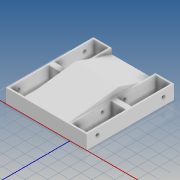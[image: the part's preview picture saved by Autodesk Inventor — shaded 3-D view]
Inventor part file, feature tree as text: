
AUTODESK INVENTOR PART (.ipt)
format: ipt  version: 2020 (Build 240168000, 168)  size: 294,400 bytes
history: native  units: mm
features: extrude x12, sketch x10
ambient origin geometry x8: Origin, YZ Plane, XZ Plane, XY Plane, X Axis, Y Axis, Z Axis, Center Point
bodies: Solid1 (feature_tree)
feature tree (22):
  extrude  "Extrusion1"  Depth=156.0mm
  extrude  "Extrusion2"  Depth=3.0mm
  extrude  "Extrusion3"  Depth=3.0mm
  extrude  "Extrusion4"  Depth=3.0mm
  extrude  "Extrusion5"  Depth=3.0mm
  extrude  "Extrusion6"  Depth=12.0mm TaperAngle=0.0deg
  extrude  "Extrusion7"  Depth=12.0mm
  extrude  "Extrusion8"  Depth=70.0mm
  extrude  "Extrusion9"  Depth=3.0mm TaperAngle=0.0deg
  sketch  "Sketch13"  dims[d22=27.0mm d23=0.0mm d24=3.0mm d25=0.0mm]
  extrude  "Extrusion10"  Depth=12.0mm
  extrude  "Extrusion11"  Depth=70.0mm
  extrude  "Extrusion12"  Depth=27.0mm TaperAngle=0.0deg
  sketch  "Sketch1"  dims[d0=84.0mm d1=156.0mm]
  sketch  "Sketch2"  dims[d2=3.0mm d3=3.0mm]
  sketch  "Sketch5"  dims[d4=3.0mm d5=3.0mm]
  sketch  "Sketch6"  dims[d6=15.0mm d7=0.0mm d8=3.0mm]
  sketch  "Sketch9"  dims[d9=3.0mm d10=3.0mm]
  sketch  "Sketch10"  dims[d11=3.0mm d12=12.0mm d13=0.0mm]
  sketch  "Sketch11"  dims[d18=3.0mm d19=12.0mm]
  sketch  "Sketch12"  dims[d20=70.0mm d21=70.0mm]
  sketch  "Sketch15"  dims[d35=70.0mm d38=12.0mm d39=70.0mm d40=27.0mm d41=0.0mm d42=3.0mm d43=0.0mm d44=10.0mm d45=0.0mm d57=10.0mm d58=0.0mm d74=10.0mm d75=0.0mm d88=10.0mm d89=0.0mm d90=10.0mm d91=0.0mm d96=10.0mm d97=0.0mm d98=19.0mm d99=0.0mm d100=11.2mm d101=6.0mm d102=19.0mm d103=11.2mm d104=6.0mm d105=55.0mm d106=10.0mm d107=5.0mm d108=15.0mm d109=10.0mm d110=5.0mm d111=15.0mm d112=10.0mm d113=5.0mm d114=15.0mm d115=10.0mm d116=5.0mm d117=19.0mm d118=11.2mm d119=6.0mm d120=19.0mm d121=11.2mm d122=6.0mm]
